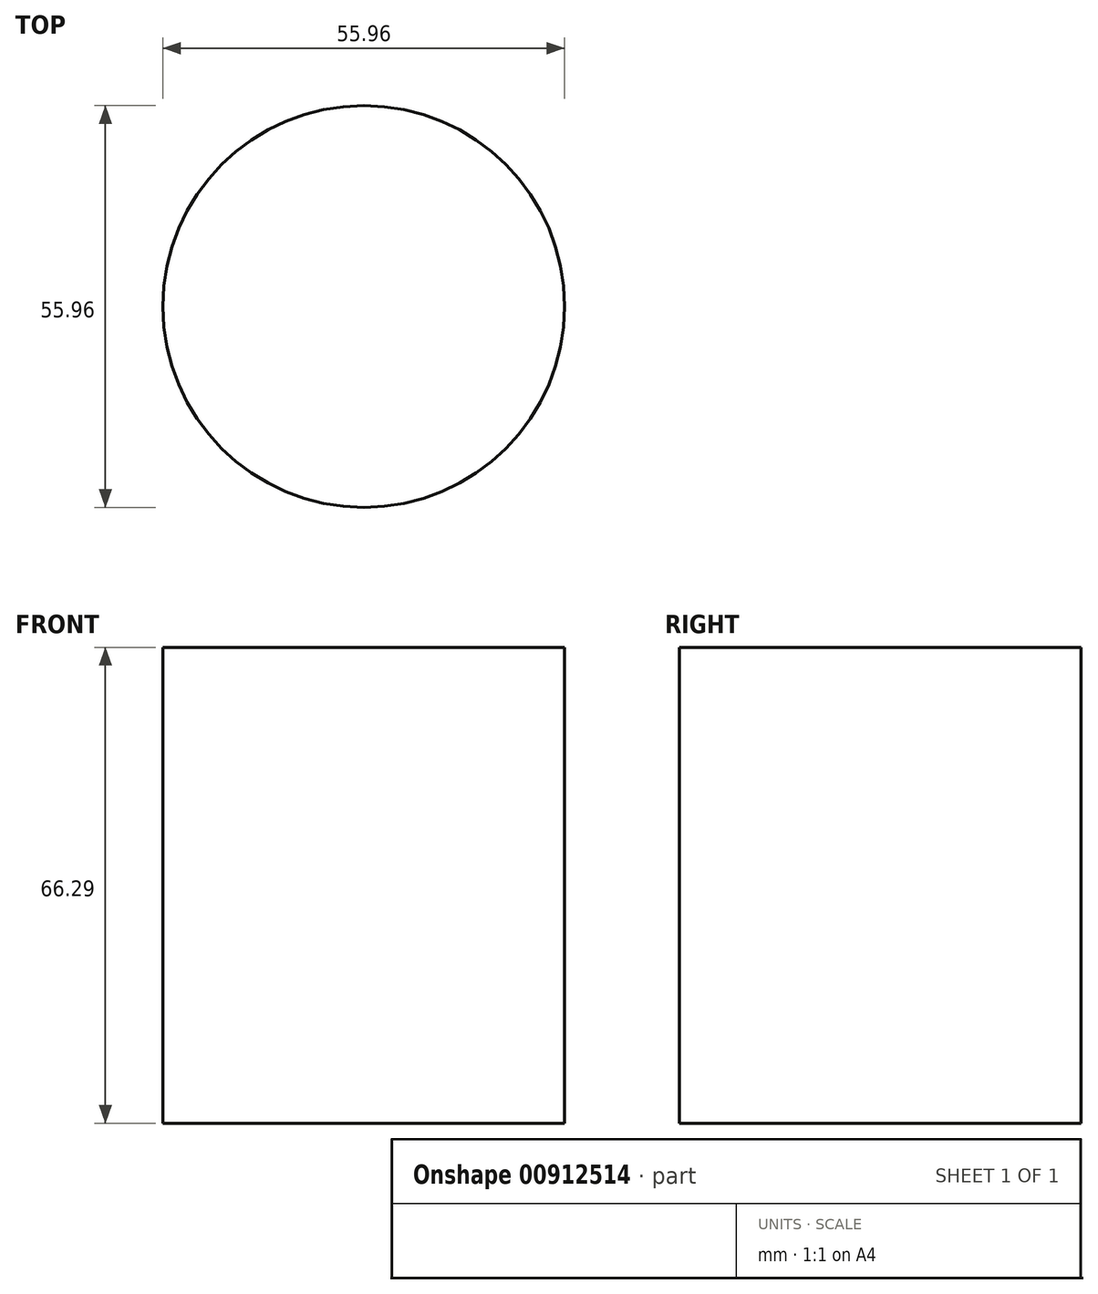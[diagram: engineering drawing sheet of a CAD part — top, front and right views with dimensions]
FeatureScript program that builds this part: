
annotation { "Feature Type Name" : "Feature", "Feature Type Description" : "" }
export const myFeature = defineFeature(function(context is Context, id is Id, definition is map)
    precondition{}
    {
        {
            var Q0;
            Q0=qCreatedBy(makeId("Top.planeOp"),FACE);
            var sketch = newSketch(context, id + "F0", { "sketchPlane" : qUnion([Q0])});
            skCircle(sketch, "E0", {"center": v(0, 0) * mm, "radius": 27.98 * mm});
            skSolve(sketch);
        }
        {
            var Q0;
            Q0=makeQuery(id+"F0.imprint","IMPRINT",FACE,{"disambiguationData":[TD([[makeQuery(id+"F0.imprint","IMPRINT",EDGE,{"derivedFrom":sQuery(id+"F0.wireOp",EDGE,"E0")}),1.0]])]});
            extrude(context, id + "F1", {"entities" : qUnion([Q0]), "depth" : 66.3 * mm, "offsetDistance" : 25.4 * mm});
        }
    });
